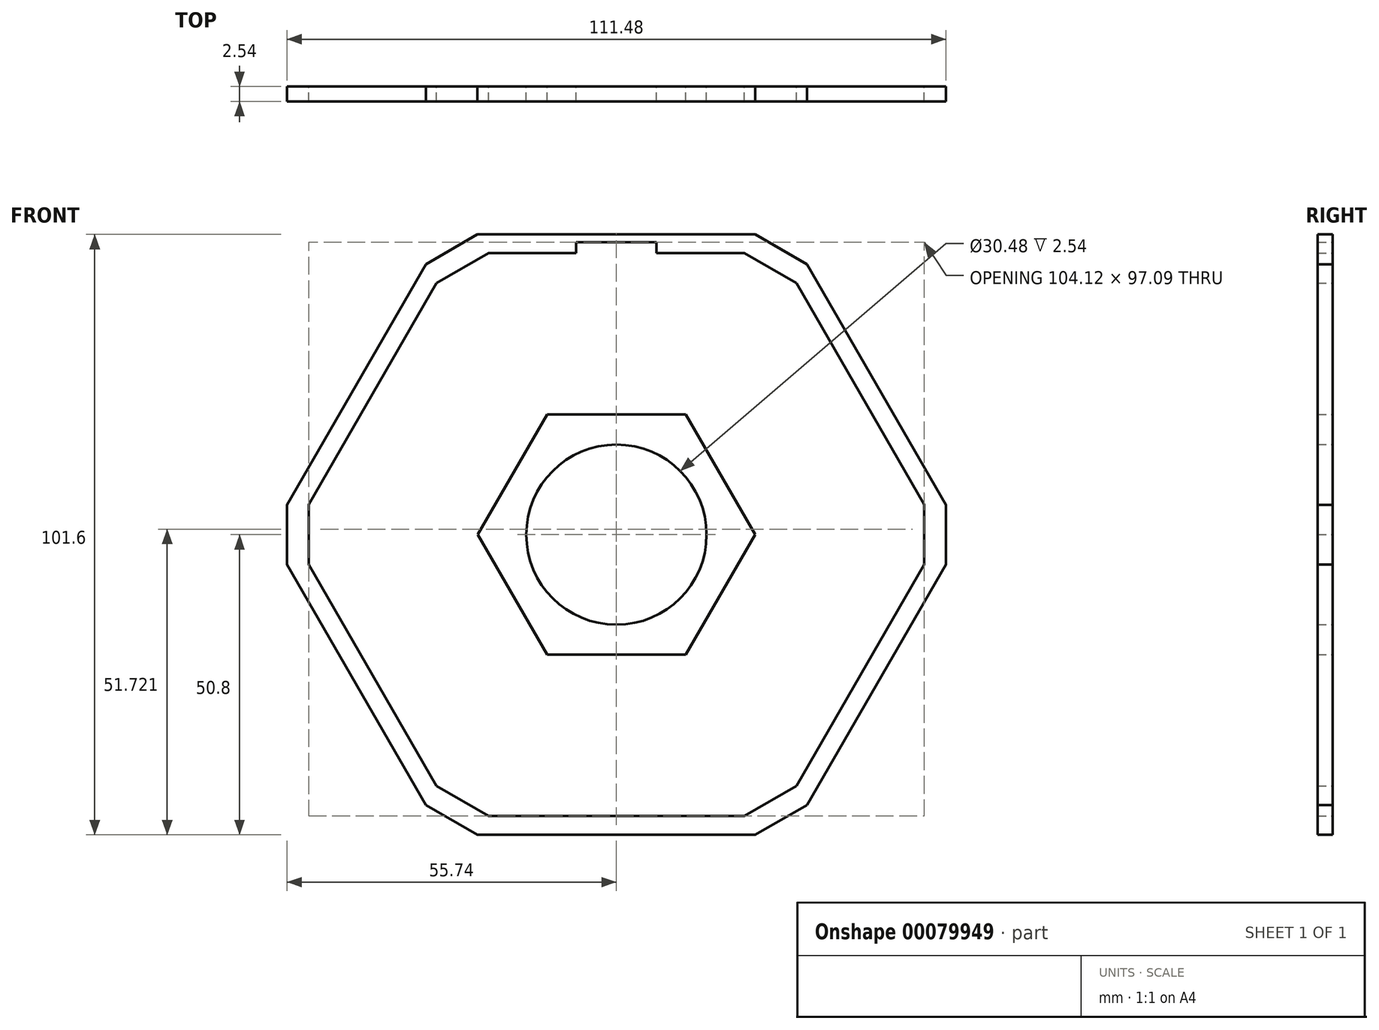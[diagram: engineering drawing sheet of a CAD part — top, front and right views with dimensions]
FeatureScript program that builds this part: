
annotation { "Feature Type Name" : "Feature", "Feature Type Description" : "" }
export const myFeature = defineFeature(function(context is Context, id is Id, definition is map)
    precondition{}
    {
        {
            var Q0;
            Q0=qCreatedBy(makeId("Front.planeOp"),FACE);
            var sketch = newSketch(context, id + "F0", { "sketchPlane" : qUnion([Q0])});
            skCircle(sketch, "E0.cCircle", {"center": v(0, 0) * mm, "radius": 50.8 * mm, "construction": true});
            skLineSegment(sketch, "E0.0", {"start": v(-29.33, 50.8) * mm, "end": v(29.33, 50.8) * mm});
            skLineSegment(sketch, "E0.1", {"start": v(29.33, 50.8) * mm, "end": v(58.66, 0) * mm});
            skLineSegment(sketch, "E0.2", {"start": v(58.66, 0) * mm, "end": v(29.33, -50.8) * mm});
            skLineSegment(sketch, "E0.3", {"start": v(29.33, -50.8) * mm, "end": v(-29.33, -50.8) * mm});
            skLineSegment(sketch, "E0.4", {"start": v(-29.33, -50.8) * mm, "end": v(-58.66, 0) * mm});
            skLineSegment(sketch, "E0.5", {"start": v(-58.66, 0) * mm, "end": v(-29.33, 50.8) * mm});
            skPoint(sketch, "E0.0.midPoint", {"position": v(0, 50.8) * mm});
            skCircle(sketch, "E1.cCircle", {"center": v(0, 0) * mm, "radius": 47.63 * mm, "construction": true});
            skLineSegment(sketch, "E1.0", {"start": v(-27.5, 47.63) * mm, "end": v(27.5, 47.63) * mm});
            skLineSegment(sketch, "E1.1", {"start": v(27.5, 47.62) * mm, "end": v(55, 0) * mm});
            skLineSegment(sketch, "E1.2", {"start": v(55, 0) * mm, "end": v(27.5, -47.63) * mm});
            skLineSegment(sketch, "E1.3", {"start": v(27.5, -47.63) * mm, "end": v(-27.5, -47.63) * mm});
            skLineSegment(sketch, "E1.4", {"start": v(-27.5, -47.63) * mm, "end": v(-55, 0) * mm});
            skLineSegment(sketch, "E1.5", {"start": v(-55, 0) * mm, "end": v(-27.5, 47.63) * mm});
            skPoint(sketch, "E1.0.midPoint", {"position": v(0, 47.63) * mm});
            skLineSegment(sketch, "E2", {"start": v(21.63, 47.63) * mm, "end": v(30.43, 42.55) * mm});
            skLineSegment(sketch, "E3", {"start": v(-21.63, 47.62) * mm, "end": v(-30.43, 42.55) * mm});
            skLineSegment(sketch, "E4", {"start": v(52.06, 5.08) * mm, "end": v(52.06, -5.08) * mm});
            skLineSegment(sketch, "E5", {"start": v(-52.06, 5.08) * mm, "end": v(-52.06, -5.08) * mm});
            skLineSegment(sketch, "E6", {"start": v(30.43, -42.55) * mm, "end": v(21.63, -47.63) * mm});
            skLineSegment(sketch, "E7", {"start": v(-21.63, -47.63) * mm, "end": v(-30.43, -42.55) * mm});
            skCircle(sketch, "E8.cCircle", {"center": v(0, 0) * mm, "radius": 20.32 * mm, "construction": true});
            skLineSegment(sketch, "E8.0", {"start": v(-11.73, 20.32) * mm, "end": v(11.73, 20.32) * mm});
            skLineSegment(sketch, "E8.1", {"start": v(11.73, 20.32) * mm, "end": v(23.46, 0) * mm});
            skLineSegment(sketch, "E8.2", {"start": v(23.46, 0) * mm, "end": v(11.73, -20.32) * mm});
            skLineSegment(sketch, "E8.3", {"start": v(11.73, -20.32) * mm, "end": v(-11.73, -20.32) * mm});
            skLineSegment(sketch, "E8.4", {"start": v(-11.73, -20.32) * mm, "end": v(-23.46, 0) * mm});
            skLineSegment(sketch, "E8.5", {"start": v(-23.46, 0) * mm, "end": v(-11.73, 20.32) * mm});
            skPoint(sketch, "E8.0.midPoint", {"position": v(0, 20.32) * mm});
            skLineSegment(sketch, "E9", {"start": v(11.73, 20.32) * mm, "end": v(23.46, 40.64) * mm});
            skLineSegment(sketch, "E10", {"start": v(23.46, 40.64) * mm, "end": v(46.93, 0) * mm});
            skLineSegment(sketch, "E11", {"start": v(46.93, 0) * mm, "end": v(23.46, 0) * mm});
            skLineSegment(sketch, "E12", {"start": v(11.73, -20.32) * mm, "end": v(23.46, -40.64) * mm});
            skLineSegment(sketch, "E13", {"start": v(23.46, -40.64) * mm, "end": v(-23.46, -40.64) * mm});
            skLineSegment(sketch, "E14", {"start": v(-23.46, -40.64) * mm, "end": v(-11.73, -20.32) * mm});
            skLineSegment(sketch, "E15", {"start": v(-11.73, 20.32) * mm, "end": v(-23.46, 40.64) * mm});
            skLineSegment(sketch, "E16", {"start": v(-23.46, 40.64) * mm, "end": v(-46.93, 0) * mm});
            skLineSegment(sketch, "E17", {"start": v(-46.93, 0) * mm, "end": v(-23.46, 0) * mm});
            skCircle(sketch, "E18", {"center": v(0, 0) * mm, "radius": 15.24 * mm});
            skPoint(sketch, "E19.middle", {"position": v(0, 42.67) * mm});
            skLineSegment(sketch, "E20", {"start": v(0, 48.26) * mm, "end": v(0, 47.63) * mm});
            skLineSegment(sketch, "E21", {"start": v(-23.46, 40.64) * mm, "end": v(-24.93, 43.18) * mm});
            skLineSegment(sketch, "E22", {"start": v(-24.93, 43.18) * mm, "end": v(-49.86, 0) * mm});
            skLineSegment(sketch, "E23", {"start": v(-49.86, 0) * mm, "end": v(-46.93, 0) * mm});
            skLineSegment(sketch, "E24", {"start": v(23.46, 40.64) * mm, "end": v(24.93, 43.18) * mm});
            skLineSegment(sketch, "E25", {"start": v(24.93, 43.18) * mm, "end": v(49.86, 0) * mm});
            skLineSegment(sketch, "E26", {"start": v(49.86, 0) * mm, "end": v(46.93, 0) * mm});
            skLineSegment(sketch, "E27", {"start": v(-23.46, -40.64) * mm, "end": v(-24.6, -42.6) * mm});
            skLineSegment(sketch, "E28", {"start": v(-24.6, -42.6) * mm, "end": v(24.6, -42.6) * mm});
            skLineSegment(sketch, "E29", {"start": v(24.6, -42.6) * mm, "end": v(23.46, -40.64) * mm});
            skLineSegment(sketch, "E30.bottom", {"start": v(-6.8, 35.88) * mm, "end": v(6.8, 35.88) * mm});
            skLineSegment(sketch, "E30.top", {"start": v(-6.8, 49.47) * mm, "end": v(6.8, 49.47) * mm});
            skLineSegment(sketch, "E30.left", {"start": v(-6.8, 35.88) * mm, "end": v(-6.8, 49.47) * mm});
            skLineSegment(sketch, "E30.right", {"start": v(6.8, 35.88) * mm, "end": v(6.8, 49.47) * mm});
            skSolve(sketch);
        }
        {
            var Q0;
            Q0=makeQuery(id+"F0.imprint","IMPRINT",FACE,{"disambiguationData":[TD([[makeQuery(id+"F0.imprint","IMPRINT",EDGE,{"derivedFrom":sQuery(id+"F0.wireOp",EDGE,"E0.0")}),-1.0]])]});
            var Q1;
            {var subQ6=sQuery(id+"F0.wireOp",EDGE,"E2");Q1=makeQuery(id+"F0.imprint","IMPRINT",FACE,{"disambiguationData":[TD([[makeQuery(id+"F0.imprint","IMPRINT",EDGE,{"derivedFrom":subQ6}),-1.0]])]});}
            var Q2;
            {var subQ3=sQuery(id+"F0.wireOp",EDGE,"E4");Q2=makeQuery(id+"F0.imprint","IMPRINT",FACE,{"disambiguationData":[TD([[makeQuery(id+"F0.imprint","IMPRINT",EDGE,{"derivedFrom":subQ3}),1.0]])]});}
            var Q3;
            {var subQ3=sQuery(id+"F0.wireOp",EDGE,"E2");Q3=makeQuery(id+"F0.imprint","IMPRINT",FACE,{"disambiguationData":[TD([[makeQuery(id+"F0.imprint","IMPRINT",EDGE,{"derivedFrom":subQ3}),1.0]])]});}
            var Q4;
            {var subQ3=sQuery(id+"F0.wireOp",EDGE,"E3");Q4=makeQuery(id+"F0.imprint","IMPRINT",FACE,{"disambiguationData":[TD([[makeQuery(id+"F0.imprint","IMPRINT",EDGE,{"derivedFrom":subQ3}),-1.0]])]});}
            var Q5;
            {var subQ3=sQuery(id+"F0.wireOp",EDGE,"E5");Q5=makeQuery(id+"F0.imprint","IMPRINT",FACE,{"disambiguationData":[TD([[makeQuery(id+"F0.imprint","IMPRINT",EDGE,{"derivedFrom":subQ3}),-1.0]])]});}
            var Q6;
            {var subQ3=sQuery(id+"F0.wireOp",EDGE,"E7");Q6=makeQuery(id+"F0.imprint","IMPRINT",FACE,{"disambiguationData":[TD([[makeQuery(id+"F0.imprint","IMPRINT",EDGE,{"derivedFrom":subQ3}),1.0]])]});}
            var Q7;
            {var subQ3=sQuery(id+"F0.wireOp",EDGE,"E6");Q7=makeQuery(id+"F0.imprint","IMPRINT",FACE,{"disambiguationData":[TD([[makeQuery(id+"F0.imprint","IMPRINT",EDGE,{"derivedFrom":subQ3}),1.0]])]});}
            var Q8;
            Q8=makeQuery(id+"F0.imprint","IMPRINT",FACE,{"disambiguationData":[TD([[makeQuery(id+"F0.imprint","IMPRINT",EDGE,{"derivedFrom":sQuery(id+"F0.wireOp",EDGE,"E8.0")}),-1.0]])]});
            extrude(context, id + "F1", {"entities" : qUnion([Q0, Q1, Q2, Q3, Q4, Q5, Q6, Q7, Q8]), "depth" : 2.54 * mm});
        }
        {
            var Q0;
            Q0=makeQuery(id+"F1.opExtrude","SWEPT_EDGE",EDGE,{"disambiguationData":[OSD([sQuery(id+"F0.wireOp",EDGE,"E0.0"),sQuery(id+"F0.wireOp",EDGE,"E0.5")])]});
            var Q1;
            Q1=makeQuery(id+"F1.opExtrude","SWEPT_EDGE",EDGE,{"disambiguationData":[OSD([sQuery(id+"F0.wireOp",EDGE,"E0.0"),sQuery(id+"F0.wireOp",EDGE,"E0.1")])]});
            var Q2;
            Q2=makeQuery(id+"F1.opExtrude","SWEPT_EDGE",EDGE,{"disambiguationData":[OSD([sQuery(id+"F0.wireOp",EDGE,"E0.1"),sQuery(id+"F0.wireOp",EDGE,"E0.2")])]});
            var Q3;
            Q3=makeQuery(id+"F1.opExtrude","SWEPT_EDGE",EDGE,{"disambiguationData":[OSD([sQuery(id+"F0.wireOp",EDGE,"E0.4"),sQuery(id+"F0.wireOp",EDGE,"E0.5")])]});
            var Q4;
            Q4=makeQuery(id+"F1.opExtrude","SWEPT_EDGE",EDGE,{"disambiguationData":[OSD([sQuery(id+"F0.wireOp",EDGE,"E0.3"),sQuery(id+"F0.wireOp",EDGE,"E0.4")])]});
            var Q5;
            Q5=makeQuery(id+"F1.opExtrude","SWEPT_EDGE",EDGE,{"disambiguationData":[OSD([sQuery(id+"F0.wireOp",EDGE,"E0.2"),sQuery(id+"F0.wireOp",EDGE,"E0.3")])]});
            chamfer(context, id + "F2", {"entities" : qUnion([Q0, Q1, Q2, Q3, Q4, Q5]), "width" : 5.84 * mm, "tangentPropagation" : true});
        }
    });
